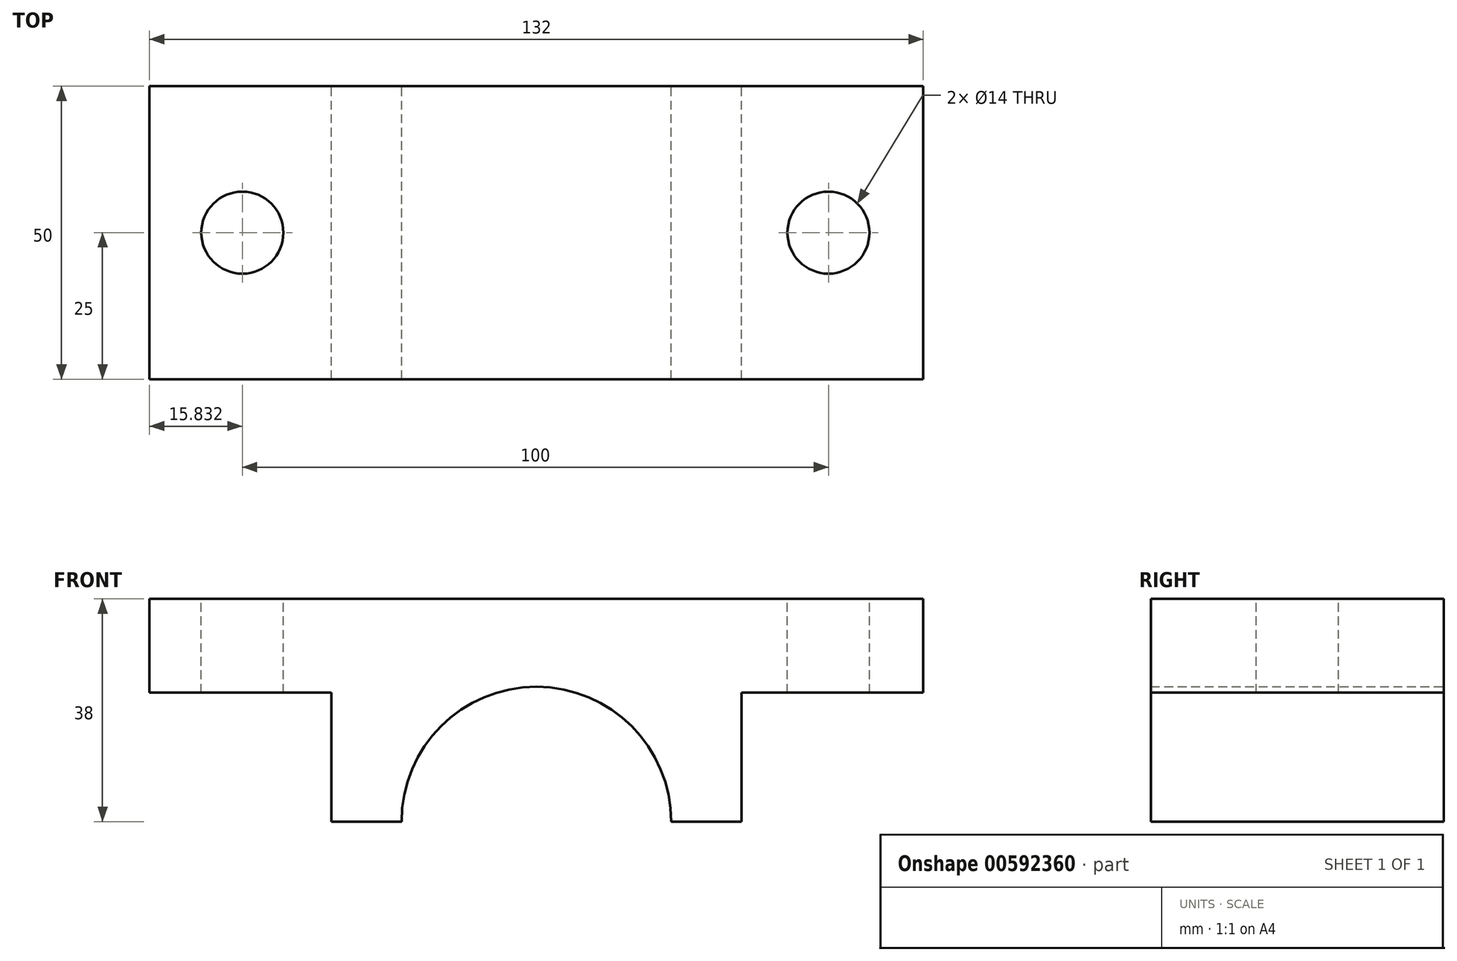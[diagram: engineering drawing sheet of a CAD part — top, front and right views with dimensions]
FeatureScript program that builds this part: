
annotation { "Feature Type Name" : "Feature", "Feature Type Description" : "" }
export const myFeature = defineFeature(function(context is Context, id is Id, definition is map)
    precondition{}
    {
        {
            var Q0;
            Q0=qCreatedBy(makeId("Front.planeOp"),FACE);
            var sketch = newSketch(context, id + "F0", { "sketchPlane" : qUnion([Q0])});
            skLineSegment(sketch, "E0", {"start": v(-35, 0) * mm, "end": v(-23, 0) * mm});
            skLineSegment(sketch, "E1", {"start": v(35, 0) * mm, "end": v(35, 22) * mm});
            skLineSegment(sketch, "E2", {"start": v(35, 22) * mm, "end": v(66, 22) * mm});
            skLineSegment(sketch, "E3", {"start": v(66, 22) * mm, "end": v(66, 38) * mm});
            skLineSegment(sketch, "E4", {"start": v(66, 38) * mm, "end": v(-66, 38) * mm});
            skLineSegment(sketch, "E5", {"start": v(-66, 38) * mm, "end": v(-66, 22) * mm});
            skLineSegment(sketch, "E6", {"start": v(-66, 22) * mm, "end": v(-35, 22) * mm});
            skLineSegment(sketch, "E7", {"start": v(-35, 22) * mm, "end": v(-35, 0) * mm});
            skArc(sketch, "E8", {"start": v(-23, 0) * mm, "mid": v(0, 23) * mm, "end": v(23, 0) * mm});
            skLineSegment(sketch, "E9.trimOffspring", {"start": v(23, 0) * mm, "end": v(35, 0) * mm});
            skSolve(sketch);
        }
        {
            var Q0;
            Q0=makeQuery(id+"F0.imprint","IMPRINT",FACE,{"disambiguationData":[TD([[makeQuery(id+"F0.imprint","IMPRINT",EDGE,{"derivedFrom":sQuery(id+"F0.wireOp",EDGE,"E0")}),1.0]])]});
            extrude(context, id + "F1", {"entities" : qUnion([Q0]), "depth" : 50 * mm, "offsetDistance" : 25 * mm});
        }
        {
            var Q0;
            Q0=makeQuery(id+"F1.opExtrude","SWEPT_FACE",FACE,{"disambiguationData":[OSD([sQuery(id+"F0.wireOp",EDGE,"E4")])]});
            var sketch = newSketch(context, id + "F2", { "sketchPlane" : qUnion([Q0])});
            skCircle(sketch, "E10", {"center": v(49.83, -25) * mm, "radius": 7 * mm});
            skCircle(sketch, "E11", {"center": v(-50.17, -25) * mm, "radius": 7 * mm});
            skSolve(sketch);
        }
        {
            var Q0;
            Q0=makeQuery(id+"F2.imprint","IMPRINT",FACE,{"disambiguationData":[TD([[makeQuery(id+"F2.imprint","IMPRINT",EDGE,{"derivedFrom":sQuery(id+"F2.wireOp",EDGE,"E10")}),1.0]])]});
            var Q1;
            Q1=makeQuery(id+"F2.imprint","IMPRINT",FACE,{"disambiguationData":[TD([[makeQuery(id+"F2.imprint","IMPRINT",EDGE,{"derivedFrom":sQuery(id+"F2.wireOp",EDGE,"E11")}),1.0]])]});
            extrude(context, id + "F3", {"entities" : qUnion([Q0, Q1]), "operationType" : NewBodyOperationType.REMOVE, "oppositeDirection" : true, "depth" : 16 * mm, "offsetDistance" : 25 * mm});
        }
    });
